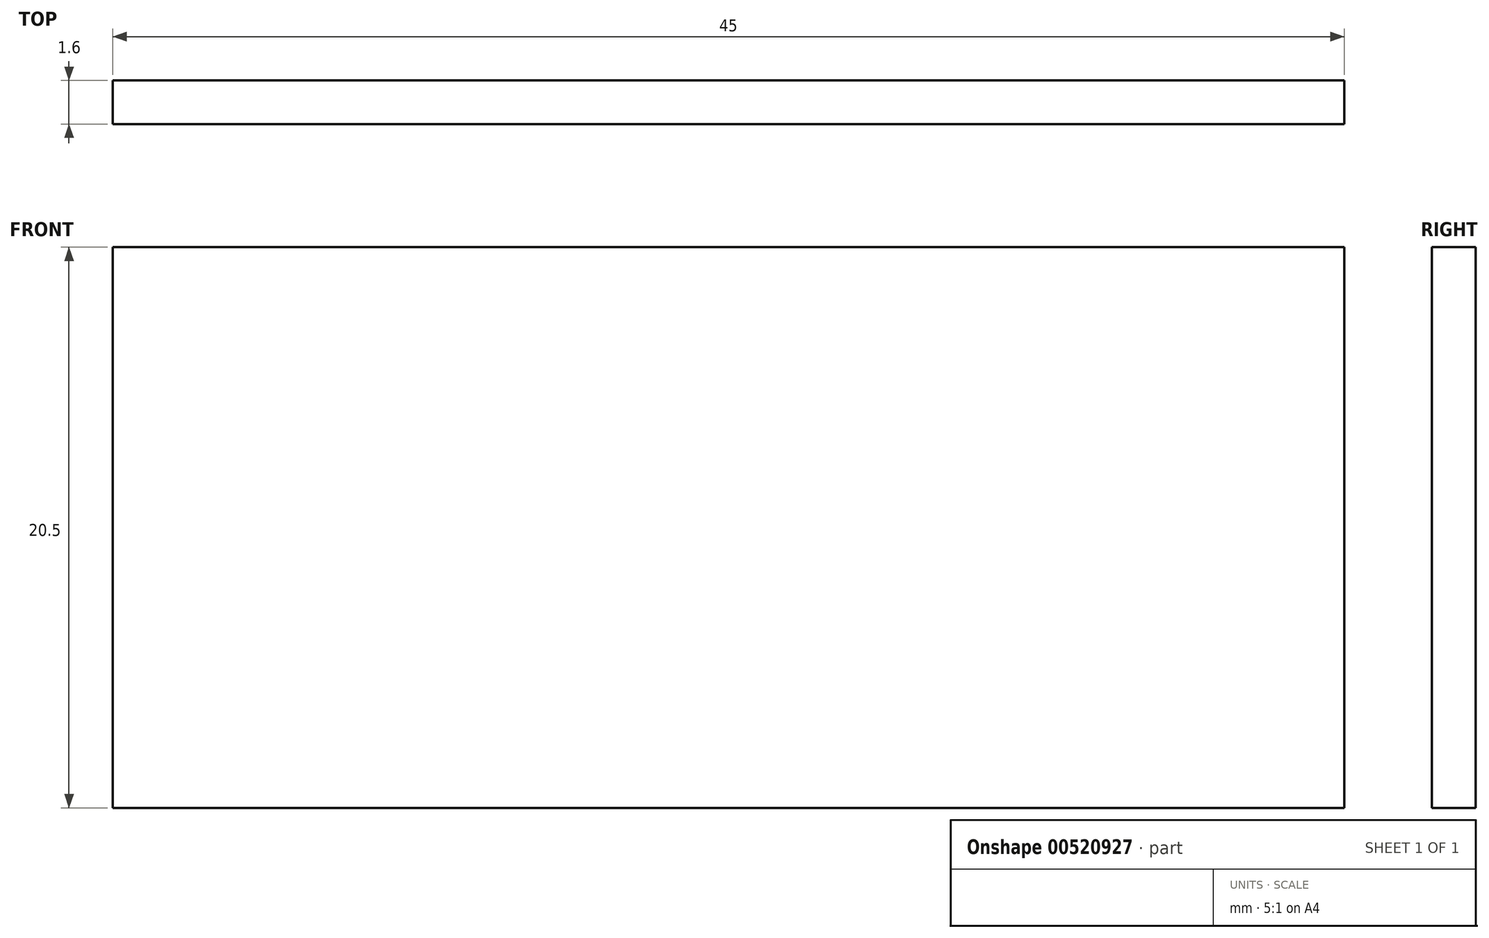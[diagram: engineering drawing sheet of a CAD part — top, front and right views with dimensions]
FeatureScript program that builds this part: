
annotation { "Feature Type Name" : "Feature", "Feature Type Description" : "" }
export const myFeature = defineFeature(function(context is Context, id is Id, definition is map)
    precondition{}
    {
        {
            var Q0;
            Q0=qCreatedBy(makeId("Front.planeOp"),FACE);
            var sketch = newSketch(context, id + "F0", { "sketchPlane" : qUnion([Q0])});
            skLineSegment(sketch, "E0.bottom", {"start": v(22.5, 10.25) * mm, "end": v(-22.5, 10.25) * mm});
            skLineSegment(sketch, "E0.top", {"start": v(22.5, -10.25) * mm, "end": v(-22.5, -10.25) * mm});
            skLineSegment(sketch, "E0.left", {"start": v(22.5, 10.25) * mm, "end": v(22.5, -10.25) * mm});
            skLineSegment(sketch, "E0.right", {"start": v(-22.5, 10.25) * mm, "end": v(-22.5, -10.25) * mm});
            skPoint(sketch, "E0.middle", {"position": v(0, 0) * mm});
            skSolve(sketch);
        }
        {
            var Q0;
            Q0 = qSketchRegion(id + "F0", true);
            extrude(context, id + "F1", {"entities" : qUnion([Q0]), "depth" : 1.6 * mm, "offsetDistance" : 25.4 * mm});
        }
    });
